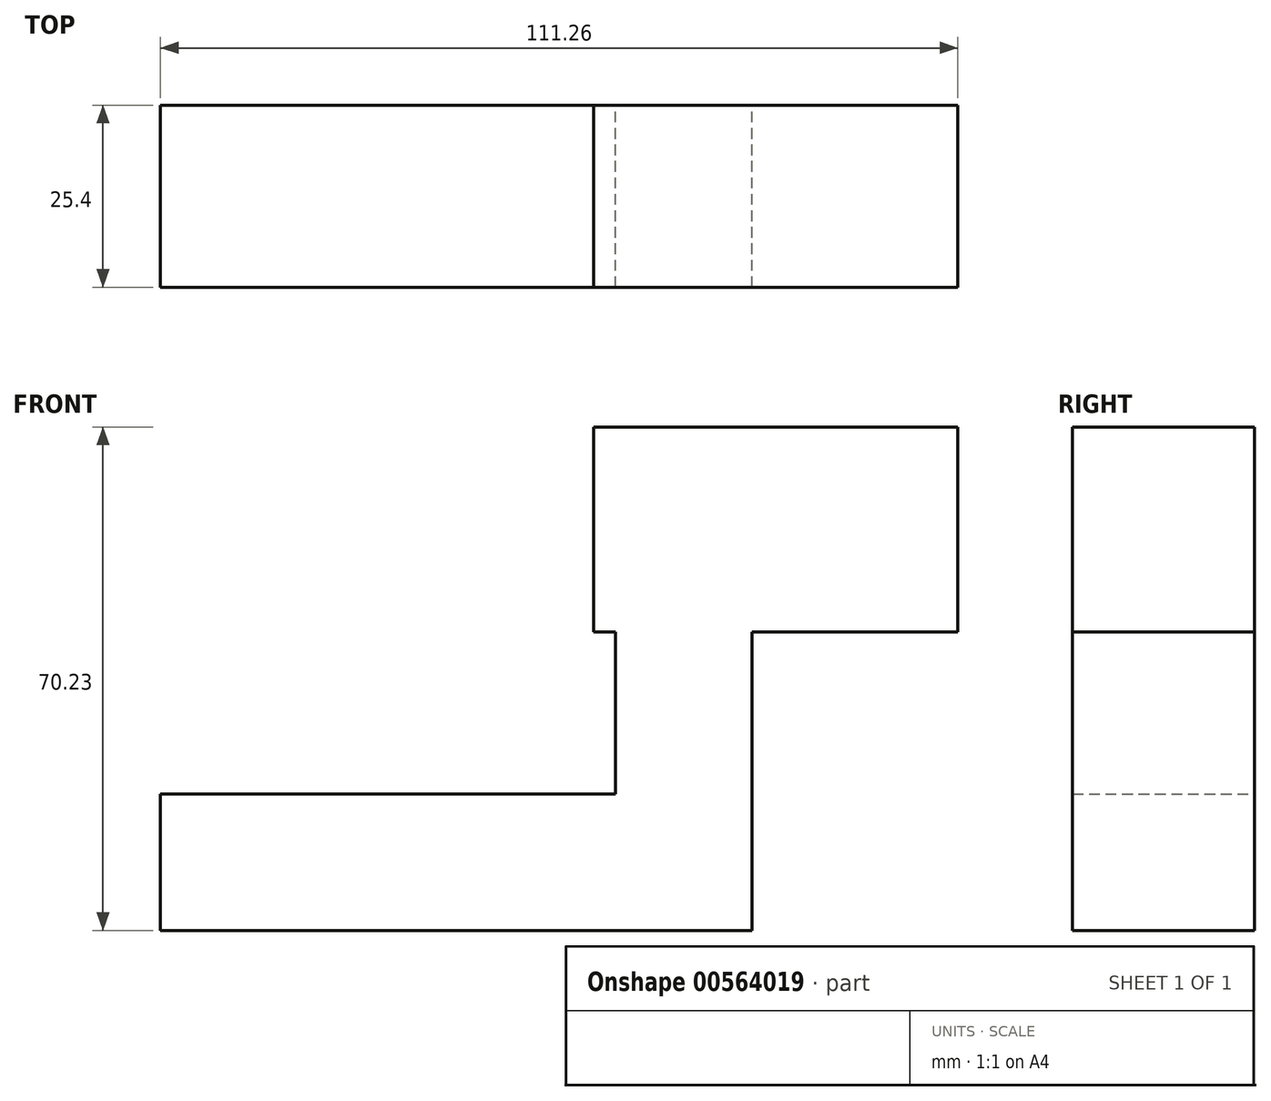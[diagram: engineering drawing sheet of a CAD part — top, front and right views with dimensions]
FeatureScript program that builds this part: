
annotation { "Feature Type Name" : "Feature", "Feature Type Description" : "" }
export const myFeature = defineFeature(function(context is Context, id is Id, definition is map)
    precondition{}
    {
        {
            var Q0;
            Q0=qCreatedBy(makeId("Front.planeOp"),FACE);
            var sketch = newSketch(context, id + "F0", { "sketchPlane" : qUnion([Q0])});
            skLineSegment(sketch, "E0.bottom", {"start": v(-41.27, -9.53) * mm, "end": v(41.28, -9.53) * mm});
            skLineSegment(sketch, "E0.top", {"start": v(-41.28, 9.53) * mm, "end": v(41.27, 9.53) * mm});
            skLineSegment(sketch, "E0.left", {"start": v(-41.27, -9.53) * mm, "end": v(-41.28, 9.53) * mm});
            skLineSegment(sketch, "E0.right", {"start": v(41.28, -9.53) * mm, "end": v(41.27, 9.53) * mm});
            skPoint(sketch, "E0.middle", {"position": v(0, 0) * mm});
            skLineSegment(sketch, "E1.bottom", {"start": v(19.19, 32.12) * mm, "end": v(69.99, 32.12) * mm});
            skLineSegment(sketch, "E1.top", {"start": v(19.19, 60.7) * mm, "end": v(69.99, 60.7) * mm});
            skLineSegment(sketch, "E1.left", {"start": v(19.19, 32.12) * mm, "end": v(19.19, 60.7) * mm});
            skLineSegment(sketch, "E1.right", {"start": v(69.99, 32.12) * mm, "end": v(69.99, 60.7) * mm});
            skPoint(sketch, "E1.middle", {"position": v(44.59, 46.4) * mm});
            skLineSegment(sketch, "E2", {"start": v(19.19, 32.12) * mm, "end": v(28.46, 32.12) * mm});
            skLineSegment(sketch, "E3", {"start": v(41.27, 9.53) * mm, "end": v(41.27, 85.72) * mm});
            skArc(sketch, "E4", {"start": v(41.27, 85.72) * mm, "mid": v(43.14, 93.2) * mm, "end": v(48.31, 98.91) * mm});
            skLineSegment(sketch, "E5", {"start": v(48.31, 98.91) * mm, "end": v(99.48, 110.22) * mm});
            skLineSegment(sketch, "E6.0", {"start": v(22.22, 9.53) * mm, "end": v(22.22, 85.72) * mm});
            skLineSegment(sketch, "E7.0", {"start": v(55.3, 86.15) * mm, "end": v(102.5, 96.58) * mm});
            skArc(sketch, "E7.1", {"start": v(55.24, 85.73) * mm, "mid": v(55.26, 85.94) * mm, "end": v(55.3, 86.15) * mm});
            skLineSegment(sketch, "E7.2", {"start": v(55.24, 9.53) * mm, "end": v(55.24, 85.73) * mm});
            skSolve(sketch);
        }
        {
            var Q0;
            Q0 = qSketchRegion(id + "F0", true);
            extrude(context, id + "F1", {"entities" : qUnion([Q0]), "depth" : 25.4 * mm, "offsetDistance" : 25.4 * mm});
        }
    });
